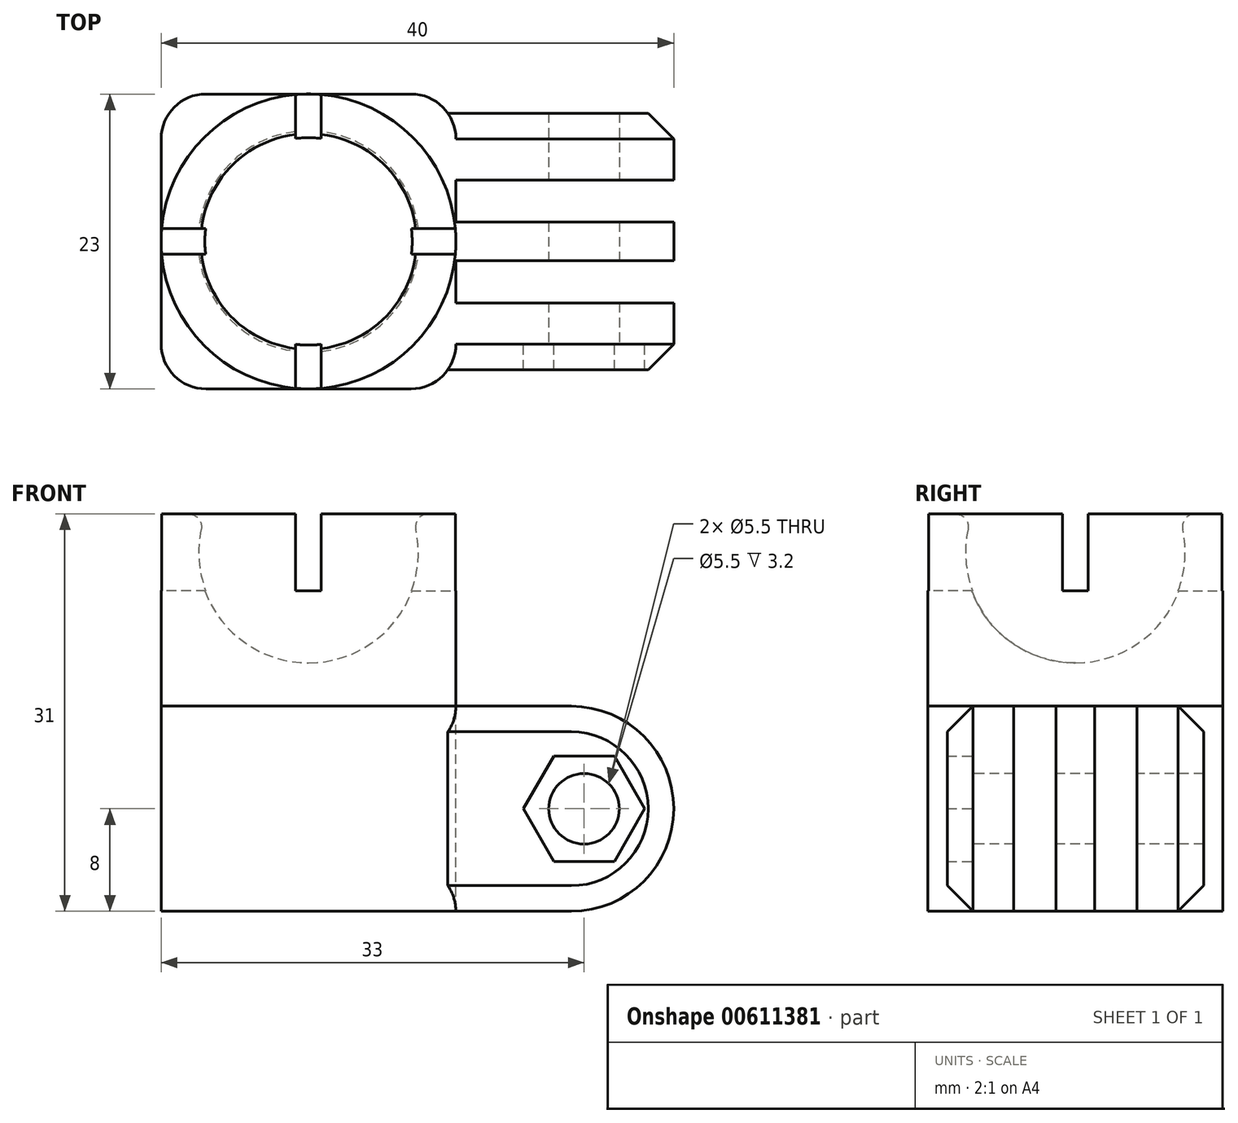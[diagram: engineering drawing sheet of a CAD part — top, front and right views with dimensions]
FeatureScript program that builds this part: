
annotation { "Feature Type Name" : "Feature", "Feature Type Description" : "" }
export const myFeature = defineFeature(function(context is Context, id is Id, definition is map)
    precondition{}
    {
        {
            var Q0;
            Q0=qCreatedBy(makeId("Top.planeOp"),FACE);
            var sketch = newSketch(context, id + "F0", { "sketchPlane" : qUnion([Q0])});
            skCircle(sketch, "E0", {"center": v(0, 0) * mm, "radius": 11.5 * mm});
            skSolve(sketch);
        }
        {
            var Q0;
            Q0=makeQuery(id+"F0.imprint","IMPRINT",FACE,{"disambiguationData":[TD([[makeQuery(id+"F0.imprint","IMPRINT",EDGE,{"derivedFrom":sQuery(id+"F0.wireOp",EDGE,"E0")}),1.0]])]});
            extrude(context, id + "F1", {"entities" : qUnion([Q0]), "depth" : 15 * mm, "offsetDistance" : 25 * mm});
        }
        {
            var Q0;
            Q0=qCreatedBy(makeId("Right.planeOp"),FACE);
            var sketch = newSketch(context, id + "F2", { "sketchPlane" : qUnion([Q0])});
            skCircle(sketch, "E1", {"center": v(0, 12) * mm, "radius": 8.62 * mm});
            skLineSegment(sketch, "E2", {"start": v(0, 3.37) * mm, "end": v(0, 20.62) * mm});
            skSolve(sketch);
        }
        {
            var Q0;
            {var subQ0=sQuery(id+"F2.wireOp",EDGE,"E2");Q0=makeQuery(id+"F2.imprint","IMPRINT",FACE,{"disambiguationData":[TD([[makeQuery(id+"F2.imprint","IMPRINT",EDGE,{"derivedFrom":subQ0}),-1.0]])]});}
            var Q1;
            Q1=sQuery(id+"F2.wireOp",EDGE,"E2");
            revolve(context, id + "F3", {"operationType" : NewBodyOperationType.REMOVE, "surfaceOperationType" : NewSurfaceOperationType.NEW, "entities" : qUnion([Q0]), "axis" : qUnion([Q1]), "revolveType" : RevolveType.FULL, "oppositeDirection" : true});
        }
        {
            var Q0;
            Q0=makeQuery(id+"F1.opExtrude","CAP_FACE",FACE,{"disambiguationData":[OSD([sQuery(id+"F0.wireOp",EDGE,"E0")])],"isStart":false});
            var sketch = newSketch(context, id + "F4", { "sketchPlane" : qUnion([Q0])});
            skLineSegment(sketch, "E3.bottom", {"start": v(-1, 0) * mm, "end": v(1, 0) * mm});
            skLineSegment(sketch, "E3.top", {"start": v(-1, 11.5) * mm, "end": v(1, 11.5) * mm});
            skLineSegment(sketch, "E3.left", {"start": v(-1, 0) * mm, "end": v(-1, 11.5) * mm});
            skLineSegment(sketch, "E3.right", {"start": v(1, 0) * mm, "end": v(1, 11.5) * mm});
            skLineSegment(sketch, "E4.1.0", {"start": v(0, -1) * mm, "end": v(0, 1) * mm});
            skLineSegment(sketch, "E4.1.1", {"start": v(-11.5, -1) * mm, "end": v(-11.5, 1) * mm});
            skLineSegment(sketch, "E4.1.2", {"start": v(0, -1) * mm, "end": v(-11.5, -1) * mm});
            skLineSegment(sketch, "E4.1.3", {"start": v(0, 1) * mm, "end": v(-11.5, 1) * mm});
            skLineSegment(sketch, "E4.2.0", {"start": v(1, 0) * mm, "end": v(-1, 0) * mm});
            skLineSegment(sketch, "E4.2.1", {"start": v(1, -11.5) * mm, "end": v(-1, -11.5) * mm});
            skLineSegment(sketch, "E4.2.2", {"start": v(1, 0) * mm, "end": v(1, -11.5) * mm});
            skLineSegment(sketch, "E4.2.3", {"start": v(-1, 0) * mm, "end": v(-1, -11.5) * mm});
            skLineSegment(sketch, "E4.3.0", {"start": v(0, 1) * mm, "end": v(0, -1) * mm});
            skLineSegment(sketch, "E4.3.1", {"start": v(11.5, 1) * mm, "end": v(11.5, -1) * mm});
            skLineSegment(sketch, "E4.3.2", {"start": v(0, 1) * mm, "end": v(11.5, 1) * mm});
            skLineSegment(sketch, "E4.3.3", {"start": v(0, -1) * mm, "end": v(11.5, -1) * mm});
            skPoint(sketch, "E4.center", {"position": v(0, 0) * mm});
            skSolve(sketch);
        }
        {
            var Q0;
            {var subQ0=sQuery(id+"F0.wireOp",EDGE,"E0");var subQ1=makeQuery(id+"F1.opExtrude","CAP_EDGE",EDGE,{"disambiguationData":[OSD([subQ0])],"isStart":false});var subQ2=makeQuery(id+"F4.imprint","INTERSECT",VERTEX,{"derivedFrom":[subQ1,sQuery(id+"F4.wireOp",EDGE,"E3.top")]});Q0=makeQuery(id+"F4.imprint","IMPRINT",FACE,{"disambiguationData":[TD([[makeQuery(id+"F4.imprint","IMPRINT",EDGE,{"disambiguationData":[TD([[subQ2,-1.0]])],"derivedFrom":subQ1}),1.0]])]});}
            var Q1;
            {var subQ0=sQuery(id+"F0.wireOp",EDGE,"E0");var subQ1=makeQuery(id+"F1.opExtrude","CAP_EDGE",EDGE,{"disambiguationData":[OSD([subQ0])],"isStart":false});var subQ2=makeQuery(id+"F4.imprint","INTERSECT",VERTEX,{"derivedFrom":[subQ1,sQuery(id+"F4.wireOp",EDGE,"E4.3.1")]});Q1=makeQuery(id+"F4.imprint","IMPRINT",FACE,{"disambiguationData":[TD([[makeQuery(id+"F4.imprint","IMPRINT",EDGE,{"disambiguationData":[TD([[subQ2,-1.0]])],"derivedFrom":subQ1}),1.0]])]});}
            var Q2;
            {var subQ0=sQuery(id+"F0.wireOp",EDGE,"E0");var subQ1=makeQuery(id+"F1.opExtrude","CAP_EDGE",EDGE,{"disambiguationData":[OSD([subQ0])],"isStart":false});var subQ2=makeQuery(id+"F4.imprint","INTERSECT",VERTEX,{"derivedFrom":[subQ1,sQuery(id+"F4.wireOp",EDGE,"E4.2.1")]});Q2=makeQuery(id+"F4.imprint","IMPRINT",FACE,{"disambiguationData":[TD([[makeQuery(id+"F4.imprint","IMPRINT",EDGE,{"disambiguationData":[TD([[subQ2,-1.0]])],"derivedFrom":subQ1}),1.0]])]});}
            var Q3;
            {var subQ0=sQuery(id+"F0.wireOp",EDGE,"E0");var subQ1=makeQuery(id+"F1.opExtrude","CAP_EDGE",EDGE,{"disambiguationData":[OSD([subQ0])],"isStart":false});var subQ2=makeQuery(id+"F4.imprint","INTERSECT",VERTEX,{"derivedFrom":[subQ1,sQuery(id+"F4.wireOp",EDGE,"E4.1.1")]});Q3=makeQuery(id+"F4.imprint","IMPRINT",FACE,{"disambiguationData":[TD([[makeQuery(id+"F4.imprint","IMPRINT",EDGE,{"disambiguationData":[TD([[subQ2,-1.0]])],"derivedFrom":subQ1}),1.0]])]});}
            extrude(context, id + "F5", {"entities" : qUnion([Q0, Q1, Q2, Q3]), "operationType" : NewBodyOperationType.REMOVE, "oppositeDirection" : true, "depth" : 6 * mm, "offsetDistance" : 25 * mm});
        }
        {
            var Q0;
            {var subQ0=makeQuery(id+"F1.opExtrude","CAP_FACE",FACE,{"disambiguationData":[OSD([sQuery(id+"F0.wireOp",EDGE,"E0")])],"isStart":false});var subQ1=makeQuery(id+"F3.opRevolve","SWEPT_FACE",FACE,{"disambiguationData":[OSD([sQuery(id+"F2.wireOp",EDGE,"E1")])]});Q0=makeQuery(id+"F5.boolean.opBoolean","SPLIT",EDGE,{"disambiguationData":[TD([makeQuery(id+"F5.opExtrude","SWEPT_FACE",FACE,{"disambiguationData":[OSD([sQuery(id+"F4.wireOp",EDGE,"E3.left")])]})])],"derivedFrom":makeQuery(id+"F3.boolean.opBoolean","INTERSECT",EDGE,{"derivedFrom":[subQ0,subQ1]})});}
            var Q1;
            {var subQ0=makeQuery(id+"F1.opExtrude","CAP_FACE",FACE,{"disambiguationData":[OSD([sQuery(id+"F0.wireOp",EDGE,"E0")])],"isStart":false});var subQ1=makeQuery(id+"F3.opRevolve","SWEPT_FACE",FACE,{"disambiguationData":[OSD([sQuery(id+"F2.wireOp",EDGE,"E1")])]});Q1=makeQuery(id+"F5.boolean.opBoolean","SPLIT",EDGE,{"disambiguationData":[TD([makeQuery(id+"F5.opExtrude","SWEPT_FACE",FACE,{"disambiguationData":[OSD([sQuery(id+"F4.wireOp",EDGE,"E3.right")])]})])],"derivedFrom":makeQuery(id+"F3.boolean.opBoolean","INTERSECT",EDGE,{"derivedFrom":[subQ0,subQ1]})});}
            var Q2;
            {var subQ0=makeQuery(id+"F1.opExtrude","CAP_FACE",FACE,{"disambiguationData":[OSD([sQuery(id+"F0.wireOp",EDGE,"E0")])],"isStart":false});var subQ1=makeQuery(id+"F3.opRevolve","SWEPT_FACE",FACE,{"disambiguationData":[OSD([sQuery(id+"F2.wireOp",EDGE,"E1")])]});Q2=makeQuery(id+"F5.boolean.opBoolean","SPLIT",EDGE,{"disambiguationData":[TD([makeQuery(id+"F5.opExtrude","SWEPT_FACE",FACE,{"disambiguationData":[OSD([sQuery(id+"F4.wireOp",EDGE,"E4.1.2")])]})])],"derivedFrom":makeQuery(id+"F3.boolean.opBoolean","INTERSECT",EDGE,{"derivedFrom":[subQ0,subQ1]})});}
            var Q3;
            {var subQ0=makeQuery(id+"F1.opExtrude","CAP_FACE",FACE,{"disambiguationData":[OSD([sQuery(id+"F0.wireOp",EDGE,"E0")])],"isStart":false});var subQ1=makeQuery(id+"F3.opRevolve","SWEPT_FACE",FACE,{"disambiguationData":[OSD([sQuery(id+"F2.wireOp",EDGE,"E1")])]});Q3=makeQuery(id+"F5.boolean.opBoolean","SPLIT",EDGE,{"disambiguationData":[TD([makeQuery(id+"F5.opExtrude","SWEPT_FACE",FACE,{"disambiguationData":[OSD([sQuery(id+"F4.wireOp",EDGE,"E4.2.2")])]})])],"derivedFrom":makeQuery(id+"F3.boolean.opBoolean","INTERSECT",EDGE,{"derivedFrom":[subQ0,subQ1]})});}
            fillet(context, id + "F6", {"entities" : qUnion([Q0, Q1, Q2, Q3]), "radius" : 1 * mm, "tangentPropagation" : true, "allowEdgeOverflow" : false});
        }
        {
            var Q0;
            Q0=makeQuery(id+"F1.opExtrude","CAP_FACE",FACE,{"disambiguationData":[OSD([sQuery(id+"F0.wireOp",EDGE,"E0")])],"isStart":true});
            var sketch = newSketch(context, id + "F7", { "sketchPlane" : qUnion([Q0])});
            skLineSegment(sketch, "E5.bottom", {"start": v(11.5, 11.5) * mm, "end": v(-11.5, 11.5) * mm});
            skLineSegment(sketch, "E5.top", {"start": v(11.5, -11.5) * mm, "end": v(-11.5, -11.5) * mm});
            skLineSegment(sketch, "E5.left", {"start": v(11.5, 11.5) * mm, "end": v(11.5, -11.5) * mm});
            skLineSegment(sketch, "E5.right", {"start": v(-11.5, 11.5) * mm, "end": v(-11.5, -11.5) * mm});
            skPoint(sketch, "E5.middle", {"position": v(0, 0) * mm});
            skSolve(sketch);
        }
        {
            var Q0;
            {var subQ0=sQuery(id+"F7.wireOp",EDGE,"E5.right");var subQ1=sQuery(id+"F7.wireOp",EDGE,"E5.bottom");var subQ2=makeQuery(id+"F7.imprint","INTERSECT",VERTEX,{"derivedFrom":[subQ1,subQ0]});Q0=makeQuery(id+"F7.imprint","IMPRINT",FACE,{"disambiguationData":[TD([[makeQuery(id+"F7.imprint","IMPRINT",EDGE,{"disambiguationData":[TD([[subQ2,1.0]])],"derivedFrom":subQ1}),1.0]])]});}
            var Q1;
            {var subQ0=sQuery(id+"F7.wireOp",EDGE,"E5.left");var subQ1=sQuery(id+"F7.wireOp",EDGE,"E5.bottom");var subQ2=makeQuery(id+"F7.imprint","INTERSECT",VERTEX,{"derivedFrom":[subQ1,subQ0]});Q1=makeQuery(id+"F7.imprint","IMPRINT",FACE,{"disambiguationData":[TD([[makeQuery(id+"F7.imprint","IMPRINT",EDGE,{"disambiguationData":[TD([[subQ2,-1.0]])],"derivedFrom":subQ1}),1.0]])]});}
            var Q2;
            {var subQ0=sQuery(id+"F7.wireOp",EDGE,"E5.left");var subQ1=sQuery(id+"F7.wireOp",EDGE,"E5.top");var subQ2=makeQuery(id+"F7.imprint","INTERSECT",VERTEX,{"derivedFrom":[subQ1,subQ0]});Q2=makeQuery(id+"F7.imprint","IMPRINT",FACE,{"disambiguationData":[TD([[makeQuery(id+"F7.imprint","IMPRINT",EDGE,{"disambiguationData":[TD([[subQ2,-1.0]])],"derivedFrom":subQ1}),-1.0]])]});}
            var Q3;
            {var subQ0=sQuery(id+"F7.wireOp",EDGE,"E5.right");var subQ1=sQuery(id+"F7.wireOp",EDGE,"E5.top");var subQ2=makeQuery(id+"F7.imprint","INTERSECT",VERTEX,{"derivedFrom":[subQ1,subQ0]});Q3=makeQuery(id+"F7.imprint","IMPRINT",FACE,{"disambiguationData":[TD([[makeQuery(id+"F7.imprint","IMPRINT",EDGE,{"disambiguationData":[TD([[subQ2,1.0]])],"derivedFrom":subQ1}),-1.0]])]});}
            var Q4;
            {var subQ0=makeQuery(id+"F1.opExtrude","CAP_EDGE",EDGE,{"disambiguationData":[OSD([sQuery(id+"F0.wireOp",EDGE,"E0")])],"isStart":true});var subQ1=makeQuery(id+"F7.imprint","INTERSECT",VERTEX,{"derivedFrom":[subQ0,sQuery(id+"F7.wireOp",EDGE,"E5.bottom")]});Q4=makeQuery(id+"F7.imprint","IMPRINT",FACE,{"disambiguationData":[TD([[makeQuery(id+"F7.imprint","IMPRINT",EDGE,{"disambiguationData":[TD([[subQ1,-1.0]])],"derivedFrom":subQ0}),-1.0]])]});}
            extrude(context, id + "F8", {"entities" : qUnion([Q0, Q1, Q2, Q3, Q4]), "operationType" : NewBodyOperationType.ADD, "depth" : 16 * mm, "offsetDistance" : 25 * mm});
        }
        {
            var Q0;
            Q0=makeQuery(id+"F8.opExtrude","SWEPT_EDGE",EDGE,{"disambiguationData":[OSD([sQuery(id+"F7.wireOp",EDGE,"E5.bottom"),sQuery(id+"F7.wireOp",EDGE,"E5.left")])]});
            var Q1;
            Q1=makeQuery(id+"F8.opExtrude","SWEPT_EDGE",EDGE,{"disambiguationData":[OSD([sQuery(id+"F7.wireOp",EDGE,"E5.bottom"),sQuery(id+"F7.wireOp",EDGE,"E5.right")])]});
            var Q2;
            Q2=makeQuery(id+"F8.opExtrude","SWEPT_EDGE",EDGE,{"disambiguationData":[OSD([sQuery(id+"F7.wireOp",EDGE,"E5.top"),sQuery(id+"F7.wireOp",EDGE,"E5.right")])]});
            var Q3;
            Q3=makeQuery(id+"F8.opExtrude","SWEPT_EDGE",EDGE,{"disambiguationData":[OSD([sQuery(id+"F7.wireOp",EDGE,"E5.top"),sQuery(id+"F7.wireOp",EDGE,"E5.left")])]});
            fillet(context, id + "F9", {"entities" : qUnion([Q0, Q1, Q2, Q3]), "radius" : 3.5 * mm, "tangentPropagation" : true, "allowEdgeOverflow" : false});
        }
        {
            var Q0;
            Q0=makeQuery(id+"F8.opExtrude","SWEPT_FACE",FACE,{"disambiguationData":[OSD([sQuery(id+"F7.wireOp",EDGE,"E5.left")])]});
            var sketch = newSketch(context, id + "F10", { "sketchPlane" : qUnion([Q0])});
            skLineSegment(sketch, "E6.bottom", {"start": v(-8, -16) * mm, "end": v(-4.8, -16) * mm});
            skLineSegment(sketch, "E6.top", {"start": v(-8, 0) * mm, "end": v(-4.8, 0) * mm});
            skLineSegment(sketch, "E6.left", {"start": v(-8, -16) * mm, "end": v(-8, 0) * mm});
            skLineSegment(sketch, "E6.right", {"start": v(-4.8, -16) * mm, "end": v(-4.8, 0) * mm});
            skLineSegment(sketch, "E7.bottom", {"start": v(-4.8, -16) * mm, "end": v(-1.5, -16) * mm});
            skLineSegment(sketch, "E7.top", {"start": v(-4.8, 0) * mm, "end": v(-1.5, 0) * mm});
            skLineSegment(sketch, "E7.right", {"start": v(-1.5, -16) * mm, "end": v(-1.5, 0) * mm});
            skLineSegment(sketch, "E8.bottom", {"start": v(-1.5, -16) * mm, "end": v(1.5, -16) * mm});
            skLineSegment(sketch, "E8.top", {"start": v(-1.5, 0) * mm, "end": v(1.5, 0) * mm});
            skLineSegment(sketch, "E8.right", {"start": v(1.5, -16) * mm, "end": v(1.5, 0) * mm});
            skLineSegment(sketch, "E9.bottom", {"start": v(1.5, -16) * mm, "end": v(4.8, -16) * mm});
            skLineSegment(sketch, "E9.top", {"start": v(1.5, 0) * mm, "end": v(4.8, 0) * mm});
            skLineSegment(sketch, "E9.right", {"start": v(4.8, -16) * mm, "end": v(4.8, 0) * mm});
            skLineSegment(sketch, "E10.bottom", {"start": v(4.8, -16) * mm, "end": v(8, -16) * mm});
            skLineSegment(sketch, "E10.top", {"start": v(4.8, 0) * mm, "end": v(8, 0) * mm});
            skLineSegment(sketch, "E10.right", {"start": v(8, -16) * mm, "end": v(8, 0) * mm});
            skSolve(sketch);
        }
        {
            var Q0;
            Q0=makeQuery(id+"F10.imprint","IMPRINT",FACE,{"disambiguationData":[TD([[makeQuery(id+"F10.imprint","IMPRINT",EDGE,{"derivedFrom":sQuery(id+"F10.wireOp",EDGE,"E6.bottom")}),1.0]])]});
            var Q1;
            Q1=makeQuery(id+"F10.imprint","IMPRINT",FACE,{"disambiguationData":[TD([[makeQuery(id+"F10.imprint","IMPRINT",EDGE,{"derivedFrom":sQuery(id+"F10.wireOp",EDGE,"E8.bottom")}),1.0]])]});
            var Q2;
            Q2=makeQuery(id+"F10.imprint","IMPRINT",FACE,{"disambiguationData":[TD([[makeQuery(id+"F10.imprint","IMPRINT",EDGE,{"derivedFrom":sQuery(id+"F10.wireOp",EDGE,"E10.bottom")}),1.0]])]});
            extrude(context, id + "F11", {"entities" : qUnion([Q0, Q1, Q2]), "operationType" : NewBodyOperationType.ADD, "depth" : 17 * mm, "offsetDistance" : 25 * mm});
        }
        {
            var Q0;
            Q0=makeQuery(id+"F11.opExtrude","SWEPT_FACE",FACE,{"disambiguationData":[OSD([sQuery(id+"F10.wireOp",EDGE,"E6.left")])]});
            var sketch = newSketch(context, id + "F12", { "sketchPlane" : qUnion([Q0])});
            skCircle(sketch, "E11", {"center": v(21.5, -8) * mm, "radius": 2.75 * mm});
            skCircle(sketch, "E12.cCircle", {"center": v(21.5, -8) * mm, "radius": 4.1 * mm, "construction": true});
            skLineSegment(sketch, "E12.0", {"start": v(23.87, -3.9) * mm, "end": v(26.23, -8) * mm});
            skLineSegment(sketch, "E12.1", {"start": v(26.23, -8) * mm, "end": v(23.87, -12.1) * mm});
            skLineSegment(sketch, "E12.2", {"start": v(23.87, -12.1) * mm, "end": v(19.13, -12.1) * mm});
            skLineSegment(sketch, "E12.3", {"start": v(19.13, -12.1) * mm, "end": v(16.77, -8) * mm});
            skLineSegment(sketch, "E12.4", {"start": v(16.77, -8) * mm, "end": v(19.13, -3.9) * mm});
            skLineSegment(sketch, "E12.5", {"start": v(19.13, -3.9) * mm, "end": v(23.87, -3.9) * mm});
            skPoint(sketch, "E12.0.midPoint", {"position": v(25.05, -5.95) * mm});
            skLineSegment(sketch, "E13.0", {"start": v(18.27, -13.6) * mm, "end": v(15.03, -8) * mm});
            skLineSegment(sketch, "E13.1", {"start": v(18.27, -2.4) * mm, "end": v(24.73, -2.4) * mm});
            skLineSegment(sketch, "E13.2", {"start": v(24.73, -2.4) * mm, "end": v(27.97, -8) * mm});
            skLineSegment(sketch, "E13.3", {"start": v(15.03, -8) * mm, "end": v(18.27, -2.4) * mm});
            skLineSegment(sketch, "E13.4", {"start": v(27.97, -8) * mm, "end": v(24.73, -13.6) * mm});
            skLineSegment(sketch, "E13.5", {"start": v(24.73, -13.6) * mm, "end": v(18.27, -13.6) * mm});
            skSolve(sketch);
        }
        {
            var Q0;
            Q0=makeQuery(id+"F12.imprint","IMPRINT",FACE,{"disambiguationData":[TD([[makeQuery(id+"F12.imprint","IMPRINT",EDGE,{"derivedFrom":sQuery(id+"F12.wireOp",EDGE,"E11")}),1.0]])]});
            extrude(context, id + "F13", {"entities" : qUnion([Q0]), "operationType" : NewBodyOperationType.REMOVE, "endBound" : BoundingType.THROUGH_ALL, "oppositeDirection" : true, "depth" : 25 * mm, "offsetDistance" : 25 * mm});
        }
        {
            var Q0;
            Q0=makeQuery(id+"F12.imprint","IMPRINT",FACE,{"disambiguationData":[TD([[makeQuery(id+"F12.imprint","IMPRINT",EDGE,{"derivedFrom":sQuery(id+"F12.wireOp",EDGE,"E12.0")}),1.0]])]});
            extrude(context, id + "F14", {"entities" : qUnion([Q0]), "operationType" : NewBodyOperationType.ADD, "depth" : 2 * mm, "offsetDistance" : 25 * mm});
        }
        {
            var Q0;
            Q0=makeQuery(id+"F11.opExtrude","SWEPT_FACE",FACE,{"disambiguationData":[OSD([sQuery(id+"F10.wireOp",EDGE,"E10.right")])]});
            extrude(context, id + "F15", {"entities" : qUnion([Q0]), "operationType" : NewBodyOperationType.ADD, "depth" : 2 * mm, "offsetDistance" : 25 * mm});
        }
        {
            var Q0;
            Q0=makeQuery(id+"F12.imprint","IMPRINT",FACE,{"disambiguationData":[TD([[makeQuery(id+"F12.imprint","IMPRINT",EDGE,{"derivedFrom":sQuery(id+"F12.wireOp",EDGE,"E13.0")}),1.0]])]});
            extrude(context, id + "F16", {"entities" : qUnion([Q0]), "operationType" : NewBodyOperationType.ADD, "depth" : 2 * mm, "offsetDistance" : 25 * mm});
        }
        {
            var Q0;
            Q0=makeQuery(id+"F16.opExtrude","SWEPT_FACE",FACE,{"disambiguationData":[OSD([sQuery(id+"F7.wireOp",EDGE,"E5.bottom"),sQuery(id+"F7.wireOp",EDGE,"E5.left"),sQuery(id+"F10.wireOp",EDGE,"E6.left")])]});
            var Q1;
            Q1=makeQuery(id+"F15.opExtrude","SWEPT_FACE",FACE,{"disambiguationData":[OSD([sQuery(id+"F7.wireOp",EDGE,"E5.top"),sQuery(id+"F7.wireOp",EDGE,"E5.left"),sQuery(id+"F10.wireOp",EDGE,"E10.right")])]});
            extrude(context, id + "F17", {"entities" : qUnion([Q0, Q1]), "operationType" : NewBodyOperationType.ADD, "endBound" : BoundingType.UP_TO_NEXT, "depth" : 25 * mm, "offsetDistance" : 25 * mm});
        }
        {
            var Q0;
            {var subQ0=sQuery(id+"F10.wireOp",EDGE,"E6.bottom");Q0=makeQuery(id+"F16.boolean.opBoolean","MERGE",EDGE,{"derivedFrom":[makeQuery(id+"F11.opExtrude","CAP_EDGE",EDGE,{"disambiguationData":[OSD([subQ0])],"isStart":false}),makeQuery(id+"F16.opExtrude","SWEPT_EDGE",EDGE,{"disambiguationData":[OSD([subQ0,sQuery(id+"F10.wireOp",EDGE,"E6.left")])]})]});}
            var Q1;
            Q1=makeQuery(id+"F11.opExtrude","CAP_EDGE",EDGE,{"disambiguationData":[OSD([sQuery(id+"F10.wireOp",EDGE,"E8.bottom")])],"isStart":false});
            var Q2;
            {var subQ0=sQuery(id+"F10.wireOp",EDGE,"E10.bottom");Q2=makeQuery(id+"F15.boolean.opBoolean","MERGE",EDGE,{"derivedFrom":[makeQuery(id+"F11.opExtrude","CAP_EDGE",EDGE,{"disambiguationData":[OSD([subQ0])],"isStart":false}),makeQuery(id+"F15.opExtrude","SWEPT_EDGE",EDGE,{"disambiguationData":[OSD([subQ0,sQuery(id+"F10.wireOp",EDGE,"E10.right")])]})]});}
            var Q3;
            {var subQ0=sQuery(id+"F10.wireOp",EDGE,"E10.top");Q3=makeQuery(id+"F15.boolean.opBoolean","MERGE",EDGE,{"derivedFrom":[makeQuery(id+"F11.opExtrude","CAP_EDGE",EDGE,{"disambiguationData":[OSD([subQ0])],"isStart":false}),makeQuery(id+"F15.opExtrude","SWEPT_EDGE",EDGE,{"disambiguationData":[OSD([subQ0,sQuery(id+"F10.wireOp",EDGE,"E10.right")])]})]});}
            var Q4;
            Q4=makeQuery(id+"F11.opExtrude","CAP_EDGE",EDGE,{"disambiguationData":[OSD([sQuery(id+"F10.wireOp",EDGE,"E8.top")])],"isStart":false});
            var Q5;
            {var subQ0=sQuery(id+"F10.wireOp",EDGE,"E6.top");Q5=makeQuery(id+"F16.boolean.opBoolean","MERGE",EDGE,{"derivedFrom":[makeQuery(id+"F11.opExtrude","CAP_EDGE",EDGE,{"disambiguationData":[OSD([subQ0])],"isStart":false}),makeQuery(id+"F16.opExtrude","SWEPT_EDGE",EDGE,{"disambiguationData":[OSD([subQ0,sQuery(id+"F10.wireOp",EDGE,"E6.left")])]})]});}
            fillet(context, id + "F18", {"entities" : qUnion([Q0, Q1, Q2, Q3, Q4, Q5]), "radius" : 8 * mm, "tangentPropagation" : true, "allowEdgeOverflow" : false});
        }
        {
            var Q0;
            {var subQ0=sQuery(id+"F10.wireOp",EDGE,"E6.left");var subQ1=sQuery(id+"F10.wireOp",EDGE,"E6.bottom");Q0=makeQuery(id+"F17.boolean.opBoolean","MERGE",EDGE,{"derivedFrom":[makeQuery(id+"F16.opExtrude","CAP_EDGE",EDGE,{"disambiguationData":[OSD([subQ1,subQ0])],"isStart":false}),makeQuery(id+"F17.opExtrude","SWEPT_EDGE",EDGE,{"disambiguationData":[OSD([sQuery(id+"F7.wireOp",EDGE,"E5.bottom"),sQuery(id+"F7.wireOp",EDGE,"E5.left"),subQ1,subQ0])]})]});}
            var Q1;
            Q1=makeQuery(id+"F16.opExtrude","CAP_EDGE",EDGE,{"disambiguationData":[OSD([sQuery(id+"F10.wireOp",EDGE,"E6.left")])],"isStart":false});
            var Q2;
            {var subQ0=sQuery(id+"F10.wireOp",EDGE,"E6.left");var subQ1=sQuery(id+"F10.wireOp",EDGE,"E6.top");Q2=makeQuery(id+"F17.boolean.opBoolean","MERGE",EDGE,{"derivedFrom":[makeQuery(id+"F16.opExtrude","CAP_EDGE",EDGE,{"disambiguationData":[OSD([subQ1,subQ0])],"isStart":false}),makeQuery(id+"F17.opExtrude","SWEPT_EDGE",EDGE,{"disambiguationData":[OSD([sQuery(id+"F7.wireOp",EDGE,"E5.bottom"),sQuery(id+"F7.wireOp",EDGE,"E5.left"),subQ1,subQ0])]})]});}
            var Q3;
            {var subQ0=sQuery(id+"F10.wireOp",EDGE,"E10.right");var subQ1=sQuery(id+"F10.wireOp",EDGE,"E10.bottom");Q3=makeQuery(id+"F17.boolean.opBoolean","MERGE",EDGE,{"derivedFrom":[makeQuery(id+"F15.opExtrude","CAP_EDGE",EDGE,{"disambiguationData":[OSD([subQ1,subQ0])],"isStart":false}),makeQuery(id+"F17.opExtrude","SWEPT_EDGE",EDGE,{"disambiguationData":[OSD([sQuery(id+"F7.wireOp",EDGE,"E5.bottom"),sQuery(id+"F7.wireOp",EDGE,"E5.top"),sQuery(id+"F7.wireOp",EDGE,"E5.left"),sQuery(id+"F7.wireOp",EDGE,"E5.right"),subQ1,subQ0])]})]});}
            var Q4;
            Q4=makeQuery(id+"F15.opExtrude","CAP_EDGE",EDGE,{"disambiguationData":[OSD([sQuery(id+"F10.wireOp",EDGE,"E10.right")])],"isStart":false});
            var Q5;
            {var subQ0=sQuery(id+"F10.wireOp",EDGE,"E10.right");var subQ1=sQuery(id+"F10.wireOp",EDGE,"E10.top");Q5=makeQuery(id+"F17.boolean.opBoolean","MERGE",EDGE,{"derivedFrom":[makeQuery(id+"F15.opExtrude","CAP_EDGE",EDGE,{"disambiguationData":[OSD([subQ1,subQ0])],"isStart":false}),makeQuery(id+"F17.opExtrude","SWEPT_EDGE",EDGE,{"disambiguationData":[OSD([sQuery(id+"F7.wireOp",EDGE,"E5.bottom"),sQuery(id+"F7.wireOp",EDGE,"E5.top"),sQuery(id+"F7.wireOp",EDGE,"E5.left"),sQuery(id+"F7.wireOp",EDGE,"E5.right"),subQ1,subQ0])]})]});}
            chamfer(context, id + "F19", {"entities" : qUnion([Q0, Q1, Q2, Q3, Q4, Q5]), "width" : 2 * mm, "tangentPropagation" : true});
        }
    });
